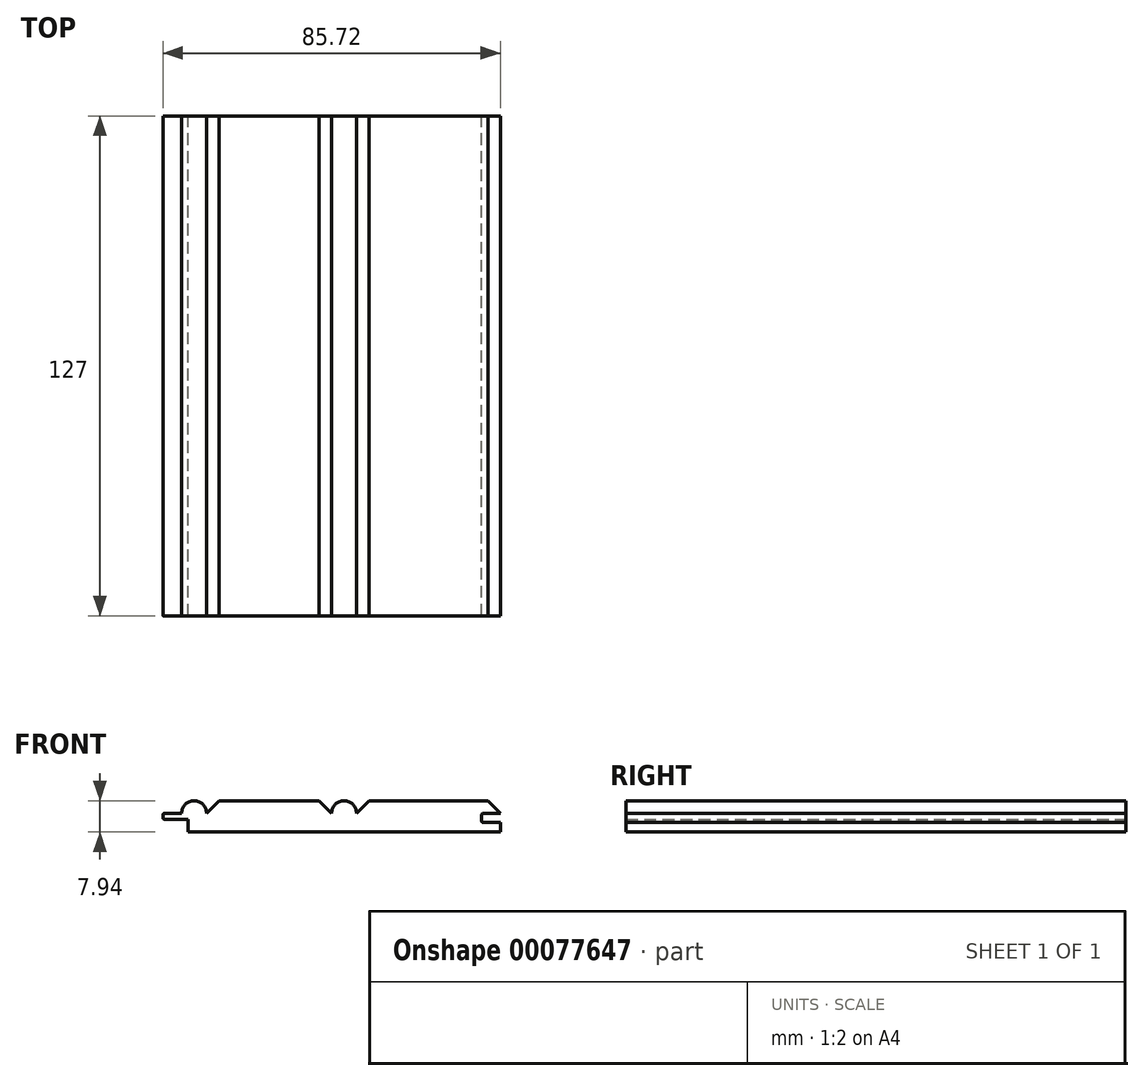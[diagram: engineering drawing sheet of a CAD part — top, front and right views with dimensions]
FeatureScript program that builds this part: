
annotation { "Feature Type Name" : "Feature", "Feature Type Description" : "" }
export const myFeature = defineFeature(function(context is Context, id is Id, definition is map)
    precondition{}
    {
        {
            var Q0;
            Q0=qCreatedBy(makeId("Front.planeOp"),FACE);
            var sketch = newSketch(context, id + "F0", { "sketchPlane" : qUnion([Q0])});
            skLineSegment(sketch, "E0", {"start": v(-36.51, -3.97) * mm, "end": v(42.86, -3.97) * mm});
            skLineSegment(sketch, "E1", {"start": v(42.86, -3.97) * mm, "end": v(42.86, -1.59) * mm});
            skLineSegment(sketch, "E2", {"start": v(39.69, 3.97) * mm, "end": v(9.52, 3.97) * mm});
            skLineSegment(sketch, "E3", {"start": v(-42.86, 0.29) * mm, "end": v(-42.86, -0.29) * mm});
            skLineSegment(sketch, "E4", {"start": v(-36.51, -3.97) * mm, "end": v(-36.51, -0.8) * mm});
            skLineSegment(sketch, "E5", {"start": v(-42.35, -0.8) * mm, "end": v(-36.51, -0.8) * mm});
            skLineSegment(sketch, "E6", {"start": v(-42.35, 0.8) * mm, "end": v(-38.1, 0.8) * mm});
            skArc(sketch, "E7", {"start": v(-42.86, -0.29) * mm, "mid": v(-42.71, -0.64) * mm, "end": v(-42.35, -0.8) * mm});
            skArc(sketch, "E8", {"start": v(-42.35, 0.8) * mm, "mid": v(-42.71, 0.64) * mm, "end": v(-42.86, 0.29) * mm});
            skArc(sketch, "E9", {"start": v(-34.93, 3.97) * mm, "mid": v(-37.17, 3.04) * mm, "end": v(-38.1, 0.8) * mm});
            skArc(sketch, "E10", {"start": v(-31.75, 0.8) * mm, "mid": v(-32.68, 3.04) * mm, "end": v(-34.93, 3.97) * mm});
            skLineSegment(sketch, "E11", {"start": v(-31.75, 0.8) * mm, "end": v(-28.58, 3.97) * mm});
            skArc(sketch, "E12", {"start": v(6.35, 0.8) * mm, "mid": v(5.42, 3.04) * mm, "end": v(3.18, 3.97) * mm});
            skArc(sketch, "E13", {"start": v(3.18, 3.97) * mm, "mid": v(0.93, 3.04) * mm, "end": v(0, 0.8) * mm});
            skLineSegment(sketch, "E14", {"start": v(0, 0.8) * mm, "end": v(-3.18, 3.97) * mm});
            skLineSegment(sketch, "E15", {"start": v(-3.18, 3.97) * mm, "end": v(-28.58, 3.97) * mm});
            skLineSegment(sketch, "E16", {"start": v(6.35, 0.8) * mm, "end": v(9.52, 3.97) * mm});
            skLineSegment(sketch, "E17", {"start": v(42.86, 0.8) * mm, "end": v(39.69, 3.97) * mm});
            skLineSegment(sketch, "E18", {"start": v(38.6, -1.59) * mm, "end": v(42.86, -1.59) * mm});
            skLineSegment(sketch, "E19", {"start": v(38.6, 0.8) * mm, "end": v(42.86, 0.8) * mm});
            skLineSegment(sketch, "E20", {"start": v(38.1, 0.29) * mm, "end": v(38.1, -1.08) * mm});
            skArc(sketch, "E21", {"start": v(38.6, 0.8) * mm, "mid": v(38.25, 0.64) * mm, "end": v(38.1, 0.29) * mm});
            skArc(sketch, "E22", {"start": v(38.1, -1.08) * mm, "mid": v(38.25, -1.44) * mm, "end": v(38.6, -1.59) * mm});
            skSolve(sketch);
        }
        {
            var Q0;
            Q0=makeQuery(id+"F0.imprint","IMPRINT",FACE,{"disambiguationData":[TD([[makeQuery(id+"F0.imprint","IMPRINT",EDGE,{"derivedFrom":sQuery(id+"F0.wireOp",EDGE,"E0")}),1.0]])]});
            extrude(context, id + "F1", {"entities" : qUnion([Q0]), "depth" : 127 * mm});
        }
    });
